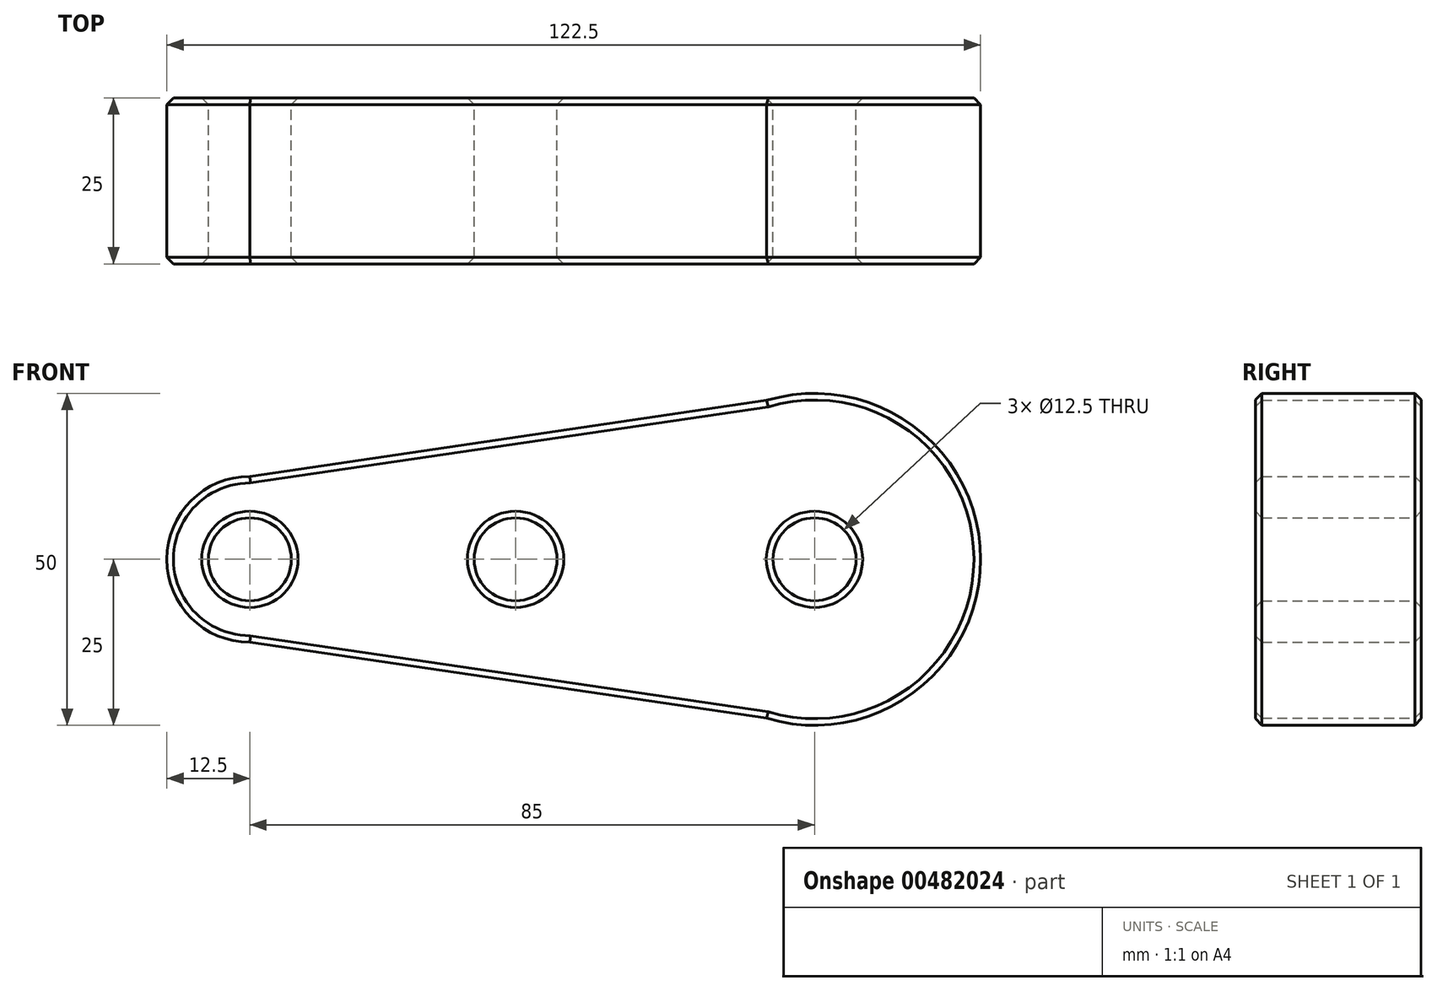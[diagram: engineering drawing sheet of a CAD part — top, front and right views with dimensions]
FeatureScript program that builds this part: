
annotation { "Feature Type Name" : "Feature", "Feature Type Description" : "" }
export const myFeature = defineFeature(function(context is Context, id is Id, definition is map)
    precondition{}
    {
        {
            var Q0;
            Q0=qCreatedBy(makeId("Front.planeOp"),FACE);
            var sketch = newSketch(context, id + "F0", { "sketchPlane" : qUnion([Q0])});
            skCircle(sketch, "E0", {"center": v(0, 0) * mm, "radius": 25 * mm});
            skCircle(sketch, "E1", {"center": v(-85, 0) * mm, "radius": 12.5 * mm});
            skLineSegment(sketch, "E2", {"start": v(0, 25) * mm, "end": v(-85, 12.5) * mm});
            skLineSegment(sketch, "E3", {"start": v(0, -25) * mm, "end": v(-85, -12.5) * mm});
            skCircle(sketch, "E4", {"center": v(0, 0) * mm, "radius": 6.25 * mm});
            skCircle(sketch, "E5", {"center": v(-45, 0) * mm, "radius": 6.25 * mm});
            skCircle(sketch, "E6", {"center": v(-85, 0) * mm, "radius": 6.25 * mm});
            skSolve(sketch);
        }
        {
            var Q0;
            Q0 = qSketchRegion(id + "F0", true);
            extrude(context, id + "F1", {"entities" : qUnion([Q0]), "depth" : 25 * mm});
        }
        {
            var Q0;
            Q0=makeQuery(id+"F1.opExtrude","CAP_FACE",FACE,{"disambiguationData":[OSD([sQuery(id+"F0.wireOp",EDGE,"E0"),sQuery(id+"F0.wireOp",EDGE,"E1"),sQuery(id+"F0.wireOp",EDGE,"E2"),sQuery(id+"F0.wireOp",EDGE,"E3"),sQuery(id+"F0.wireOp",EDGE,"E4"),sQuery(id+"F0.wireOp",EDGE,"E5"),sQuery(id+"F0.wireOp",EDGE,"E6")])],"isStart":false});
            chamfer(context, id + "F2", {"entities" : qUnion([Q0]), "width" : 1 * mm, "tangentPropagation" : true});
        }
        {
            var Q0;
            Q0=makeQuery(id+"F1.opExtrude","CAP_FACE",FACE,{"disambiguationData":[OSD([sQuery(id+"F0.wireOp",EDGE,"E0"),sQuery(id+"F0.wireOp",EDGE,"E1"),sQuery(id+"F0.wireOp",EDGE,"E2"),sQuery(id+"F0.wireOp",EDGE,"E3"),sQuery(id+"F0.wireOp",EDGE,"E4"),sQuery(id+"F0.wireOp",EDGE,"E5"),sQuery(id+"F0.wireOp",EDGE,"E6")])],"isStart":true});
            chamfer(context, id + "F3", {"entities" : qUnion([Q0]), "width" : 1 * mm, "tangentPropagation" : true});
        }
    });
